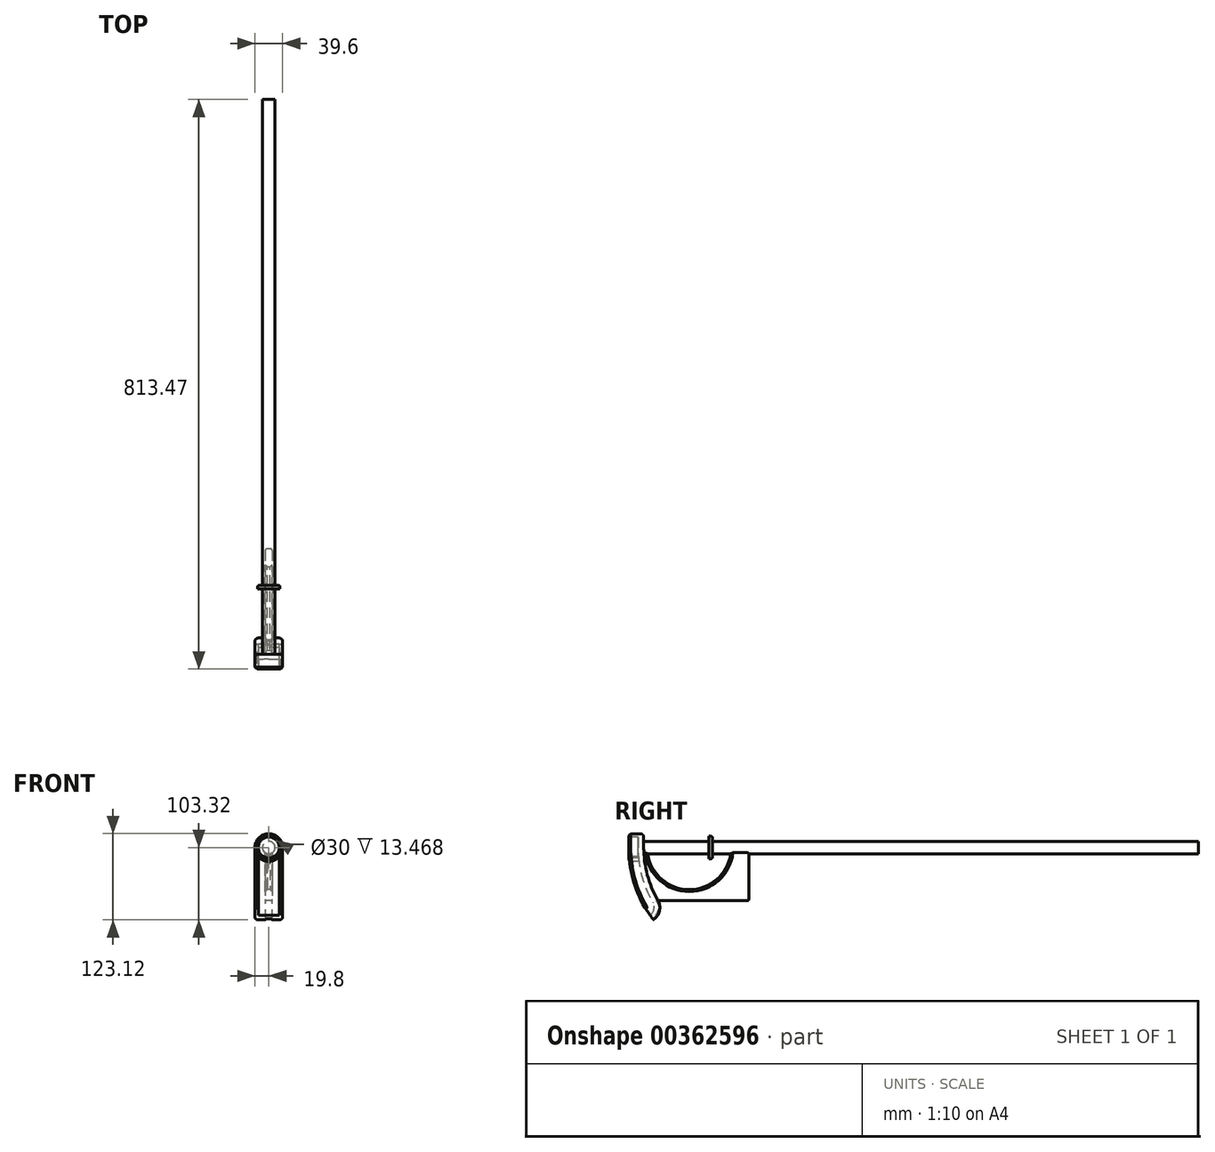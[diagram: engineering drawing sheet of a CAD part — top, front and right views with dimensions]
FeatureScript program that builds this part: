
annotation { "Feature Type Name" : "Feature", "Feature Type Description" : "" }
export const myFeature = defineFeature(function(context is Context, id is Id, definition is map)
    precondition{}
    {
        {
            var Q0;
            Q0=qCreatedBy(makeId("Front.planeOp"),FACE);
            var sketch = newSketch(context, id + "F0", { "sketchPlane" : qUnion([Q0])});
            skCircle(sketch, "E0", {"center": v(0, 0) * mm, "radius": 9 * mm});
            skCircle(sketch, "E1", {"center": v(0, 0) * mm, "radius": 16 * mm});
            skSolve(sketch);
        }
        {
            var Q0;
            Q0=makeQuery(id+"F0.imprint","IMPRINT",FACE,{"disambiguationData":[TD([[makeQuery(id+"F0.imprint","IMPRINT",EDGE,{"derivedFrom":sQuery(id+"F0.wireOp",EDGE,"E0")}),1.0]])]});
            extrude(context, id + "F1", {"entities" : qUnion([Q0]), "oppositeDirection" : true, "depth" : 800 * mm});
        }
        {
            var Q0;
            Q0=makeQuery(id+"F1.opExtrude","SWEPT_BODY",BODY,{"disambiguationData":[OSD([sQuery(id+"F0.wireOp",EDGE,"E0")])]});
            transform(context, id + "F2", {"entities" : qUnion([Q0]), "transformType" : TransformType.TRANSLATION_3D, "dx" : 0 * mm, "dy" : -158 * mm, "dz" : 0 * mm, "makeCopy" : false});
        }
        {
            var Q0;
            Q0=makeQuery(id+"F0.imprint","IMPRINT",FACE,{"disambiguationData":[TD([[makeQuery(id+"F0.imprint","IMPRINT",EDGE,{"derivedFrom":sQuery(id+"F0.wireOp",EDGE,"E0")}),-1.0]])]});
            extrude(context, id + "F3", {"entities" : qUnion([Q0]), "depth" : 5 * mm});
        }
        {
            var Q0;
            Q0=makeQuery(id+"F3.opExtrude","SWEPT_BODY",BODY,{"disambiguationData":[OSD([sQuery(id+"F0.wireOp",EDGE,"E0"),sQuery(id+"F0.wireOp",EDGE,"E1")])]});
            transform(context, id + "F4", {"entities" : qUnion([Q0]), "transformType" : TransformType.TRANSLATION_3D, "dx" : 0 * mm, "dy" : -52 * mm, "dz" : 0 * mm, "makeCopy" : false});
        }
        {
            var Q0;
            Q0=qCreatedBy(makeId("Right.planeOp"),FACE);
            var sketch = newSketch(context, id + "F5", { "sketchPlane" : qUnion([Q0])});
            skArc(sketch, "E2", {"start": v(-152, 0) * mm, "mid": v(-146.82, -39.34) * mm, "end": v(-131.64, -76) * mm});
            skLineSegment(sketch, "E3", {"start": v(-152, 0) * mm, "end": v(0, 0) * mm});
            skLineSegment(sketch, "E4", {"start": v(0, 0) * mm, "end": v(-131.64, -76) * mm});
            skCircle(sketch, "E5", {"center": v(-85, 0) * mm, "radius": 60 * mm});
            skPoint(sketch, "E6", {"position": v(-145, 0) * mm});
            skLineSegment(sketch, "E7.bottom", {"start": v(0, 0) * mm, "end": v(-131.64, 0) * mm});
            skLineSegment(sketch, "E7.top", {"start": v(0, -76) * mm, "end": v(-131.64, -76) * mm});
            skLineSegment(sketch, "E7.left", {"start": v(0, 0) * mm, "end": v(0, -76) * mm});
            skLineSegment(sketch, "E7.right", {"start": v(-131.64, 0) * mm, "end": v(-131.64, -76) * mm});
            skSolve(sketch);
        }
        {
            var Q0;
            {var subQ4=sQuery(id+"F5.wireOp",EDGE,"E7.top");Q0=makeQuery(id+"F5.imprint","IMPRINT",FACE,{"disambiguationData":[TD([[makeQuery(id+"F5.imprint","IMPRINT",EDGE,{"derivedFrom":subQ4}),-1.0]])]});}
            var Q1;
            {var subQ1=sQuery(id+"F5.wireOp",EDGE,"E4");var subQ3=sQuery(id+"F5.wireOp",EDGE,"E5");var subQ4=makeQuery(id+"F5.imprint","INTERSECT",VERTEX,{"disambiguationData":[OD(1.0)],"derivedFrom":[subQ1,subQ3]});Q1=makeQuery(id+"F5.imprint","IMPRINT",FACE,{"disambiguationData":[TD([[makeQuery(id+"F5.imprint","IMPRINT",EDGE,{"disambiguationData":[TD([[subQ4,1.0]])],"derivedFrom":subQ3}),-1.0]])]});}
            var Q2;
            {var subQ0=sQuery(id+"F5.wireOp",EDGE,"E2");Q2=makeQuery(id+"F5.imprint","IMPRINT",FACE,{"disambiguationData":[TD([[makeQuery(id+"F5.imprint","IMPRINT",EDGE,{"derivedFrom":subQ0}),1.0]])]});}
            var Q3;
            {var subQ0=sQuery(id+"F5.wireOp",EDGE,"E7.bottom");var subQ3=sQuery(id+"F5.wireOp",EDGE,"E5");var subQ5=makeQuery(id+"F5.imprint","INTERSECT",VERTEX,{"derivedFrom":[subQ3,subQ0]});Q3=makeQuery(id+"F5.imprint","IMPRINT",FACE,{"disambiguationData":[TD([[makeQuery(id+"F5.imprint","IMPRINT",EDGE,{"disambiguationData":[TD([[subQ5,1.0]])],"derivedFrom":subQ3}),-1.0]])]});}
            extrude(context, id + "F6", {"entities" : qUnion([Q0, Q1, Q2, Q3]), "endBound" : BoundingType.SYMMETRIC, "depth" : 10 * mm});
        }
        {
            var Q0;
            Q0=qCreatedBy(makeId("Top.planeOp"),FACE);
            var sketch = newSketch(context, id + "F7", { "sketchPlane" : qUnion([Q0])});
            skLineSegment(sketch, "E8.bottom", {"start": v(15, -158) * mm, "end": v(-15, -158) * mm});
            skLineSegment(sketch, "E8.top", {"start": v(15, -178) * mm, "end": v(-15, -178) * mm});
            skLineSegment(sketch, "E8.left", {"start": v(15, -158) * mm, "end": v(15, -178) * mm});
            skLineSegment(sketch, "E8.right", {"start": v(-15, -158) * mm, "end": v(-15, -178) * mm});
            skPoint(sketch, "E8.middle", {"position": v(0, -168) * mm});
            skPoint(sketch, "E9", {"position": v(0, -178) * mm});
            skPoint(sketch, "E10", {"position": v(0, -160.73) * mm});
            skLineSegment(sketch, "E11.bottom", {"start": v(19.8, -150) * mm, "end": v(-19.8, -150) * mm});
            skLineSegment(sketch, "E11.top", {"start": v(19.8, -171.47) * mm, "end": v(-19.8, -171.47) * mm});
            skLineSegment(sketch, "E11.left", {"start": v(19.8, -150) * mm, "end": v(19.8, -171.47) * mm});
            skLineSegment(sketch, "E11.right", {"start": v(-19.8, -150) * mm, "end": v(-19.8, -171.47) * mm});
            skSolve(sketch);
        }
        {
            var Q0;
            {var subQ1=sQuery(id+"F7.wireOp",EDGE,"E8.bottom");Q0=makeQuery(id+"F7.imprint","IMPRINT",FACE,{"disambiguationData":[TD([[makeQuery(id+"F7.imprint","IMPRINT",EDGE,{"derivedFrom":subQ1}),-1.0]])]});}
            var Q1;
            Q1=sQuery(id+"F5.wireOp",EDGE,"E2");
            sweep(context, id + "F8", {"operationType" : NewBodyOperationType.ADD, "profiles" : qUnion([Q0]), "path" : qUnion([Q1])});
        }
        {
            var Q0;
            Q0=makeQuery(id+"F1.opExtrude","SWEPT_BODY",BODY,{"disambiguationData":[OSD([sQuery(id+"F0.wireOp",EDGE,"E0")])]});
            var Q1;
            Q1=makeQuery(id+"F3.opExtrude","SWEPT_BODY",BODY,{"disambiguationData":[OSD([sQuery(id+"F0.wireOp",EDGE,"E0"),sQuery(id+"F0.wireOp",EDGE,"E1")])]});
            var Q2;
            Q2=makeQuery(id+"F6.opExtrude","SWEPT_BODY",BODY,{"disambiguationData":[OSD([sQuery(id+"F5.wireOp",EDGE,"E2"),sQuery(id+"F5.wireOp",EDGE,"E3"),sQuery(id+"F5.wireOp",EDGE,"E5"),sQuery(id+"F5.wireOp",EDGE,"E7.bottom"),sQuery(id+"F5.wireOp",EDGE,"E7.top"),sQuery(id+"F5.wireOp",EDGE,"E7.left")])]});
            booleanBodies(context, id + "F9", {"operationType" : BooleanOperationType.UNION, "tools" : qUnion([Q0, Q1, Q2])});
        }
        {
            var Q0;
            Q0=makeQuery(id+"F8.opSweep","SWEPT_EDGE",EDGE,{"disambiguationData":[OSD([sQuery(id+"F5.wireOp",EDGE,"E2"),sQuery(id+"F7.wireOp",EDGE,"E11.bottom"),sQuery(id+"F7.wireOp",EDGE,"E11.right")])]});
            var Q1;
            Q1=makeQuery(id+"F8.opSweep","SWEPT_EDGE",EDGE,{"disambiguationData":[OSD([sQuery(id+"F5.wireOp",EDGE,"E2"),sQuery(id+"F7.wireOp",EDGE,"E11.bottom"),sQuery(id+"F7.wireOp",EDGE,"E11.left")])]});
            fillet(context, id + "F10", {"entities" : qUnion([Q0, Q1]), "radius" : 5 * mm, "tangentPropagation" : true, "allowEdgeOverflow" : false});
        }
        {
            var Q0;
            Q0=makeQuery(id+"F8.opSweep","SWEPT_EDGE",EDGE,{"disambiguationData":[OSD([sQuery(id+"F5.wireOp",EDGE,"E2"),sQuery(id+"F7.wireOp",EDGE,"E11.top"),sQuery(id+"F7.wireOp",EDGE,"E11.right")])]});
            var Q1;
            Q1=makeQuery(id+"F8.opSweep","SWEPT_EDGE",EDGE,{"disambiguationData":[OSD([sQuery(id+"F5.wireOp",EDGE,"E2"),sQuery(id+"F7.wireOp",EDGE,"E11.top"),sQuery(id+"F7.wireOp",EDGE,"E11.left")])]});
            var Q2;
            Q2=makeQuery(id+"F6.opExtrude","CAP_EDGE",EDGE,{"disambiguationData":[OSD([sQuery(id+"F5.wireOp",EDGE,"E5")])],"isStart":true});
            var Q3;
            Q3=makeQuery(id+"F6.opExtrude","CAP_EDGE",EDGE,{"disambiguationData":[OSD([sQuery(id+"F5.wireOp",EDGE,"E5")])],"isStart":false});
            chamfer(context, id + "F11", {"entities" : qUnion([Q0, Q1, Q2, Q3]), "width" : 3 * mm, "tangentPropagation" : true});
        }
        {
            var Q0;
            {var subQ0=sQuery(id+"F7.wireOp",EDGE,"E8.left");var subQ1=sQuery(id+"F5.wireOp",EDGE,"E2");var subQ2=sQuery(id+"F7.wireOp",EDGE,"E8.bottom");var subQ4=sQuery(id+"F7.wireOp",EDGE,"E11.left");var subQ5=sQuery(id+"F7.wireOp",EDGE,"E11.bottom");var subQ6=sQuery(id+"F7.wireOp",EDGE,"E11.top");Q0=makeQuery(id+"F9.opBoolean","SPLIT",FACE,{"disambiguationData":[TD([makeQuery(id+"F8.opSweep","SWEPT_FACE",FACE,{"disambiguationData":[OSD([subQ1,subQ0])]})])],"derivedFrom":makeQuery(id+"F8.boolean.opBoolean","MERGE",FACE,{"derivedFrom":[makeQuery(id+"F6.opExtrude","SWEPT_FACE",FACE,{"disambiguationData":[OSD([sQuery(id+"F5.wireOp",EDGE,"E3")])]}),makeQuery(id+"F8.opSweep","CAP_FACE",FACE,{"disambiguationData":[OSD([sQuery(id+"F5.wireOp",VERTEX,"E2.start"),subQ2,subQ0,sQuery(id+"F7.wireOp",EDGE,"E8.right"),subQ5,subQ6,subQ4,sQuery(id+"F7.wireOp",EDGE,"E11.right")])],"isStart":true})]})});}
            var Q1;
            Q1=makeQuery(id+"F9.opBoolean","SPLIT",EDGE,{"disambiguationData":[OD(1.0)],"derivedFrom":makeQuery(id+"F1.opExtrude","CAP_EDGE",EDGE,{"disambiguationData":[OSD([sQuery(id+"F0.wireOp",EDGE,"E0")])],"isStart":true})});
            sweep(context, id + "F12", {"operationType" : NewBodyOperationType.ADD, "profiles" : qUnion([Q0]), "path" : qUnion([Q1])});
        }
        {
            var Q0;
            Q0=makeQuery(id+"F3.opExtrude","CAP_EDGE",EDGE,{"disambiguationData":[OSD([sQuery(id+"F0.wireOp",EDGE,"E1")])],"isStart":true});
            var Q1;
            Q1=makeQuery(id+"F6.opExtrude","CAP_EDGE",EDGE,{"disambiguationData":[OSD([sQuery(id+"F5.wireOp",EDGE,"E7.left")])],"isStart":false});
            var Q2;
            Q2=makeQuery(id+"F6.opExtrude","CAP_EDGE",EDGE,{"disambiguationData":[OSD([sQuery(id+"F5.wireOp",EDGE,"E7.top")])],"isStart":false});
            var Q3;
            Q3=makeQuery(id+"F6.opExtrude","CAP_EDGE",EDGE,{"disambiguationData":[OSD([sQuery(id+"F5.wireOp",EDGE,"E7.top")])],"isStart":true});
            var Q4;
            Q4=makeQuery(id+"F6.opExtrude","SWEPT_EDGE",EDGE,{"disambiguationData":[OSD([sQuery(id+"F5.wireOp",EDGE,"E7.top"),sQuery(id+"F5.wireOp",EDGE,"E7.left")])]});
            var Q5;
            Q5=makeQuery(id+"F6.opExtrude","CAP_EDGE",EDGE,{"disambiguationData":[OSD([sQuery(id+"F5.wireOp",EDGE,"E7.left")])],"isStart":true});
            fillet(context, id + "F13", {"entities" : qUnion([Q0, Q1, Q2, Q3, Q4, Q5]), "radius" : 2 * mm, "tangentPropagation" : true, "allowEdgeOverflow" : false});
        }
        {
            var Q0;
            Q0=makeQuery(id+"F8.opSweep","CAP_FACE",FACE,{"disambiguationData":[OSD([sQuery(id+"F5.wireOp",VERTEX,"E2.end"),sQuery(id+"F7.wireOp",EDGE,"E8.bottom"),sQuery(id+"F7.wireOp",EDGE,"E8.left"),sQuery(id+"F7.wireOp",EDGE,"E8.right"),sQuery(id+"F7.wireOp",EDGE,"E11.bottom"),sQuery(id+"F7.wireOp",EDGE,"E11.top"),sQuery(id+"F7.wireOp",EDGE,"E11.left"),sQuery(id+"F7.wireOp",EDGE,"E11.right")])],"isStart":false});
            var Q1;
            {var subQ0=sQuery(id+"F7.wireOp",EDGE,"E11.top");var subQ1=sQuery(id+"F5.wireOp",VERTEX,"E2.end");Q1=makeQuery(id+"F8.opSweep","CAP_EDGE",EDGE,{"disambiguationData":[OSD([subQ1,subQ0]),TDD([subQ1,makeQuery(id+"F7.imprint","IMPRINT",EDGE,{"disambiguationData":[TD([[makeQuery(id+"F7.imprint","INTERSECT",VERTEX,{"derivedFrom":[subQ0,sQuery(id+"F7.wireOp",EDGE,"E11.right")]}),1.0]])],"derivedFrom":subQ0})])],"isStart":false});}
            revolve(context, id + "F14", {"operationType" : NewBodyOperationType.ADD, "entities" : qUnion([Q0]), "axis" : qUnion([Q1]), "revolveType" : RevolveType.ONE_DIRECTION, "angle" : 85 * degree});
        }
    });
